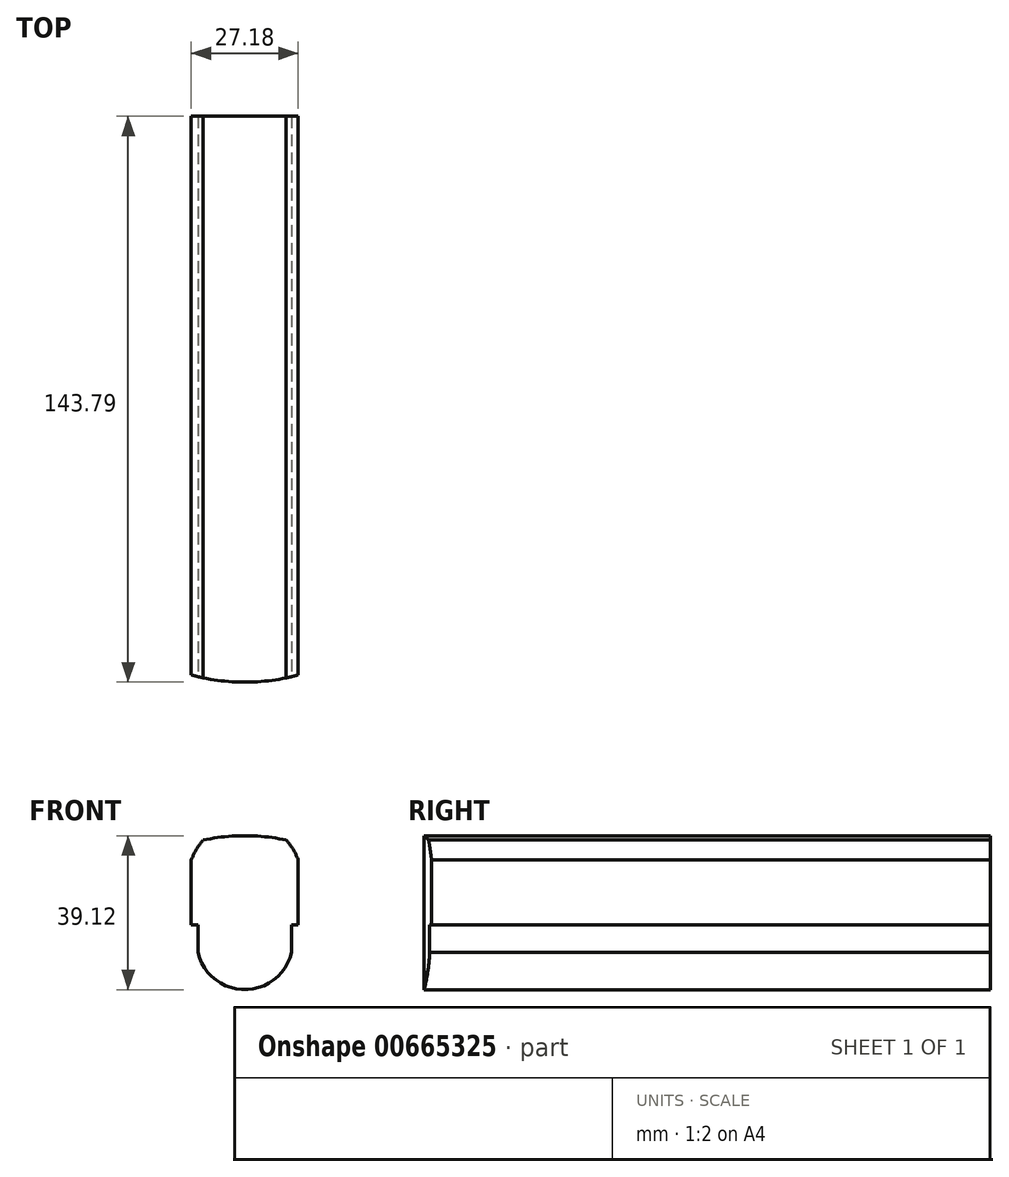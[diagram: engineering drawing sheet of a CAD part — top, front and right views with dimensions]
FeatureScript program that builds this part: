
annotation { "Feature Type Name" : "Feature", "Feature Type Description" : "" }
export const myFeature = defineFeature(function(context is Context, id is Id, definition is map)
    precondition{}
    {
        {
            var Q0;
            Q0=qCreatedBy(makeId("Front.planeOp"),FACE);
            var sketch = newSketch(context, id + "F0", { "sketchPlane" : qUnion([Q0])});
            skCircle(sketch, "E0", {"center": v(0, 0) * mm, "radius": 7.3 * mm, "construction": true});
            skCircle(sketch, "E1", {"center": v(0, -16.2) * mm, "radius": 5.46 * mm, "construction": true});
            skLineSegment(sketch, "E2.bottom", {"start": v(-13.59, -28.74) * mm, "end": v(13.59, -28.74) * mm, "construction": true});
            skLineSegment(sketch, "E2.top", {"start": v(-13.59, 10.38) * mm, "end": v(13.59, 10.38) * mm});
            skLineSegment(sketch, "E2.left", {"start": v(-13.59, -12.23) * mm, "end": v(-13.59, 10.38) * mm});
            skLineSegment(sketch, "E2.right", {"start": v(13.59, -12.23) * mm, "end": v(13.59, 10.38) * mm});
            skPoint(sketch, "E2.middle", {"position": v(0, -9.18) * mm});
            skLineSegment(sketch, "E3", {"start": v(-13.59, -12.23) * mm, "end": v(-11.87, -12.23) * mm});
            skLineSegment(sketch, "E4", {"start": v(-11.87, -12.23) * mm, "end": v(-11.87, -19.22) * mm});
            skLineSegment(sketch, "E5", {"start": v(13.59, -12.23) * mm, "end": v(11.87, -12.23) * mm});
            skLineSegment(sketch, "E6", {"start": v(11.87, -12.23) * mm, "end": v(11.87, -19.22) * mm});
            skLineSegment(sketch, "E7", {"start": v(-11.87, -12.23) * mm, "end": v(11.87, -12.23) * mm, "construction": true});
            skLineSegment(sketch, "E8", {"start": v(-11.87, -19.22) * mm, "end": v(11.87, -19.22) * mm, "construction": true});
            skArc(sketch, "E9", {"start": v(-11.87, -19.22) * mm, "mid": v(0, -28.74) * mm, "end": v(11.87, -19.22) * mm});
            skSolve(sketch);
        }
        {
            var Q0;
            Q0=makeQuery(id+"F0.imprint","IMPRINT",FACE,{"disambiguationData":[TD([[makeQuery(id+"F0.imprint","IMPRINT",EDGE,{"derivedFrom":sQuery(id+"F0.wireOp",EDGE,"E2.bottom")}),1.0]])]});
            var Q1;
            Q1=makeQuery(id+"F0.imprint","IMPRINT",FACE,{"disambiguationData":[TD([[makeQuery(id+"F0.imprint","IMPRINT",EDGE,{"derivedFrom":sQuery(id+"F0.wireOp",EDGE,"E2.top")}),-1.0]])]});
            extrude(context, id + "F1", {"entities" : qUnion([Q0, Q1]), "oppositeDirection" : true, "depth" : 143.79 * mm, "offsetDistance" : 25.4 * mm});
        }
        {
            var Q0;
            Q0=makeQuery(id+"F1.opExtrude","CAP_FACE",FACE,{"disambiguationData":[OSD([sQuery(id+"F0.wireOp",EDGE,"E2.bottom"),sQuery(id+"F0.wireOp",EDGE,"E2.top"),sQuery(id+"F0.wireOp",EDGE,"E2.left"),sQuery(id+"F0.wireOp",EDGE,"E2.right")])],"isStart":true});
            var sketch = newSketch(context, id + "F2", { "sketchPlane" : qUnion([Q0])});
            skLineSegment(sketch, "E10", {"start": v(0, 10.38) * mm, "end": v(0, -28.74) * mm, "construction": true});
            skArc(sketch, "E11", {"start": v(0, 10.38) * mm, "mid": v(-5.3, 10.1) * mm, "end": v(-10.54, 9.27) * mm});
            skArc(sketch, "E12", {"start": v(-10.54, 9.27) * mm, "mid": v(-12.3, 6.87) * mm, "end": v(-13.59, 4.2) * mm});
            skLineSegment(sketch, "E13", {"start": v(-13.59, 10.38) * mm, "end": v(0, 10.38) * mm});
            skArc(sketch, "E14", {"start": v(10.54, 9.27) * mm, "mid": v(5.3, 10.1) * mm, "end": v(0, 10.38) * mm});
            skArc(sketch, "E15", {"start": v(13.59, 4.2) * mm, "mid": v(12.3, 6.87) * mm, "end": v(10.54, 9.27) * mm});
            skLineSegment(sketch, "E16", {"start": v(13.59, 4.2) * mm, "end": v(13.59, 18.64) * mm});
            skLineSegment(sketch, "E17", {"start": v(13.59, 18.64) * mm, "end": v(-13.88, 18.64) * mm});
            skLineSegment(sketch, "E18", {"start": v(-13.88, 18.64) * mm, "end": v(-13.59, 4.2) * mm});
            skSolve(sketch);
        }
        {
            var Q0;
            Q0 = qSketchRegion(id + "F2", true);
            extrude(context, id + "F3", {"entities" : qUnion([Q0]), "operationType" : NewBodyOperationType.REMOVE, "endBound" : BoundingType.THROUGH_ALL, "oppositeDirection" : true, "depth" : 25.4 * mm, "offsetDistance" : 25.4 * mm});
        }
        {
            var Q0;
            Q0=qCreatedBy(makeId("Top.planeOp"),FACE);
            var sketch = newSketch(context, id + "F4", { "sketchPlane" : qUnion([Q0])});
            skArc(sketch, "E19", {"start": v(-13.59, 1.85) * mm, "mid": v(0, 0) * mm, "end": v(13.59, 1.85) * mm});
            skLineSegment(sketch, "E20", {"start": v(-13.59, 1.85) * mm, "end": v(13.59, 1.85) * mm, "construction": true});
            skLineSegment(sketch, "E21", {"start": v(-13.59, 1.85) * mm, "end": v(-13.59, -7.92) * mm});
            skLineSegment(sketch, "E22", {"start": v(-13.59, -7.92) * mm, "end": v(13.59, -7.92) * mm});
            skLineSegment(sketch, "E23", {"start": v(13.59, -7.92) * mm, "end": v(13.59, 1.85) * mm});
            skSolve(sketch);
        }
        {
            var Q0;
            Q0 = qSketchRegion(id + "F4", true);
            extrude(context, id + "F5", {"entities" : qUnion([Q0]), "operationType" : NewBodyOperationType.REMOVE, "endBound" : BoundingType.SYMMETRIC, "oppositeDirection" : true, "depth" : 76.2 * mm, "offsetDistance" : 25.4 * mm});
        }
    });
